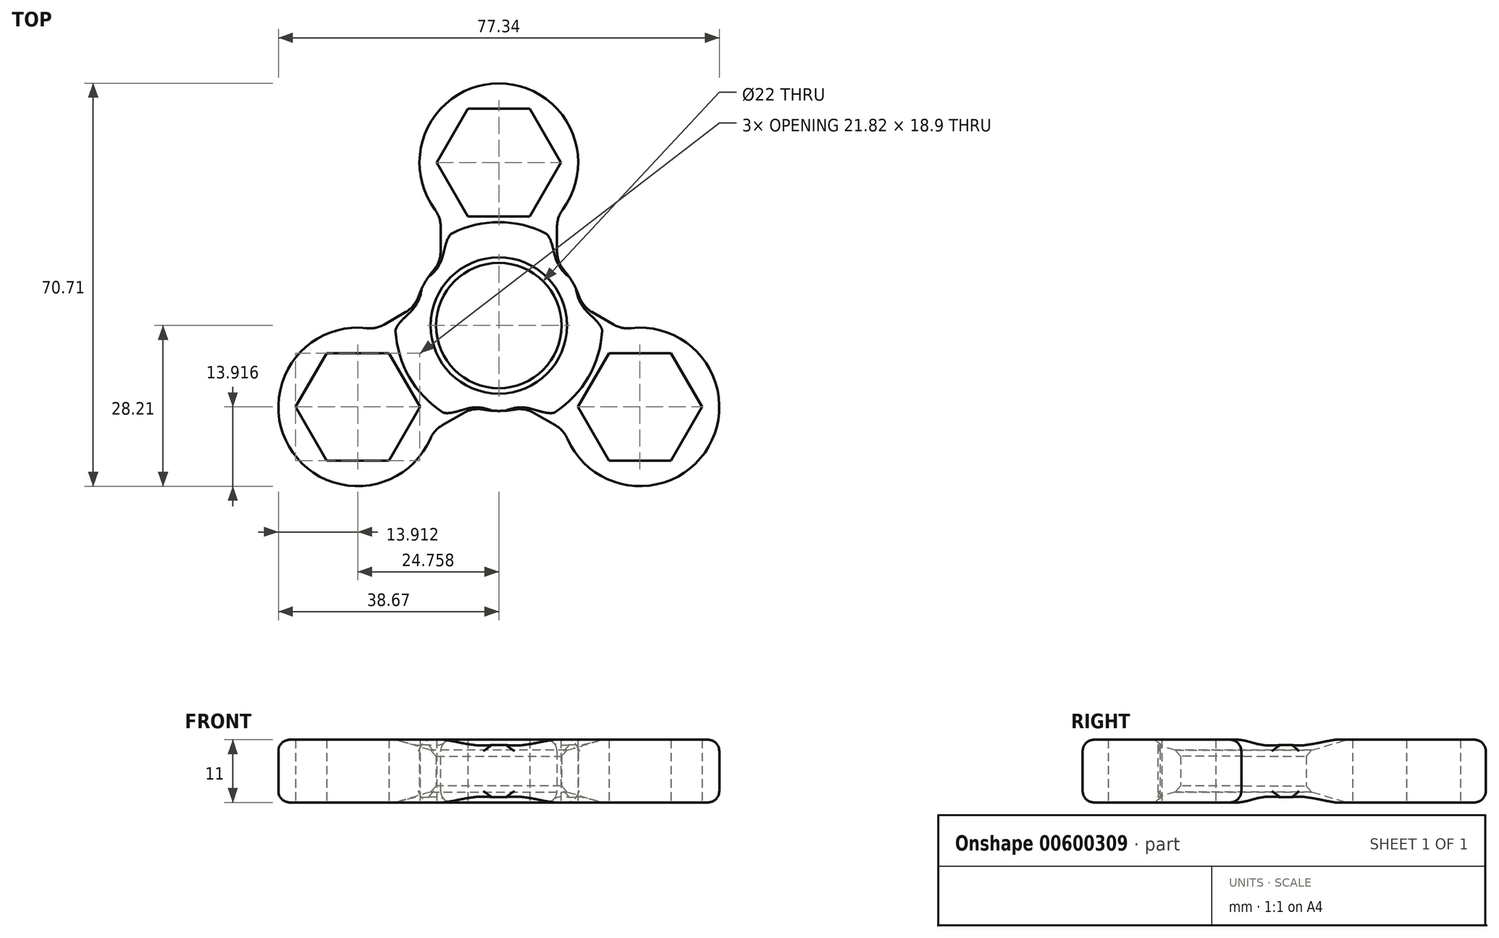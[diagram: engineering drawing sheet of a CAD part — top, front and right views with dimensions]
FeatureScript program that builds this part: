
annotation { "Feature Type Name" : "Feature", "Feature Type Description" : "" }
export const myFeature = defineFeature(function(context is Context, id is Id, definition is map)
    precondition{}
    {
        {
            var Q0;
            Q0=qCreatedBy(makeId("Top.planeOp"),FACE);
            var sketch = newSketch(context, id + "F0", { "sketchPlane" : qUnion([Q0])});
            skCircle(sketch, "E0", {"center": v(0, 0) * mm, "radius": 42.5 * mm, "construction": true});
            skLineSegment(sketch, "E1", {"start": v(0, 28.59) * mm, "end": v(0, 0) * mm, "construction": true});
            skLineSegment(sketch, "E2", {"start": v(0, 0) * mm, "end": v(-24.76, -14.3) * mm, "construction": true});
            skLineSegment(sketch, "E3", {"start": v(0, 0) * mm, "end": v(24.76, -14.3) * mm, "construction": true});
            skCircle(sketch, "E4.cCircle", {"center": v(0, 28.59) * mm, "radius": 9.45 * mm, "construction": true});
            skLineSegment(sketch, "E4.0", {"start": v(10.91, 28.59) * mm, "end": v(5.46, 19.14) * mm});
            skLineSegment(sketch, "E4.1", {"start": v(5.46, 19.14) * mm, "end": v(-5.46, 19.14) * mm});
            skLineSegment(sketch, "E4.2", {"start": v(-5.46, 19.14) * mm, "end": v(-10.91, 28.59) * mm});
            skLineSegment(sketch, "E4.3", {"start": v(-10.91, 28.59) * mm, "end": v(-5.46, 38.04) * mm});
            skLineSegment(sketch, "E4.4", {"start": v(-5.46, 38.04) * mm, "end": v(5.46, 38.04) * mm});
            skLineSegment(sketch, "E4.5", {"start": v(5.46, 38.04) * mm, "end": v(10.91, 28.59) * mm});
            skPoint(sketch, "E4.0.midPoint", {"position": v(8.18, 23.86) * mm});
            skArc(sketch, "E5.cCircle", {"start": v(10.2, 19.14) * mm, "mid": v(0, 42.5) * mm, "end": v(-10.2, 19.14) * mm});
            skLineSegment(sketch, "E6", {"start": v(-10.2, 19.14) * mm, "end": v(-10.2, 10.99) * mm});
            skLineSegment(sketch, "E7", {"start": v(10.2, 19.14) * mm, "end": v(10.2, 10.99) * mm});
            skCircle(sketch, "E8", {"center": v(0, 0) * mm, "radius": 11 * mm});
            skCircle(sketch, "E9.cCircle", {"center": v(24.76, -14.3) * mm, "radius": 9.45 * mm, "construction": true});
            skLineSegment(sketch, "E9.0", {"start": v(35.67, -14.3) * mm, "end": v(30.21, -23.74) * mm});
            skLineSegment(sketch, "E9.1", {"start": v(30.21, -23.74) * mm, "end": v(19.3, -23.74) * mm});
            skLineSegment(sketch, "E9.2", {"start": v(19.3, -23.74) * mm, "end": v(13.85, -14.3) * mm});
            skLineSegment(sketch, "E9.3", {"start": v(13.85, -14.3) * mm, "end": v(19.3, -4.84) * mm});
            skLineSegment(sketch, "E9.4", {"start": v(19.3, -4.84) * mm, "end": v(30.21, -4.84) * mm});
            skLineSegment(sketch, "E9.5", {"start": v(30.21, -4.84) * mm, "end": v(35.67, -14.3) * mm});
            skPoint(sketch, "E9.0.midPoint", {"position": v(32.94, -19.02) * mm});
            skArc(sketch, "E10.cCircle", {"start": v(11.47, -18.41) * mm, "mid": v(36.8, -21.25) * mm, "end": v(21.68, -0.73) * mm});
            skCircle(sketch, "E11.cCircle", {"center": v(-24.76, -14.3) * mm, "radius": 9.45 * mm, "construction": true});
            skLineSegment(sketch, "E11.0", {"start": v(-13.85, -14.3) * mm, "end": v(-19.3, -23.74) * mm});
            skLineSegment(sketch, "E11.1", {"start": v(-19.3, -23.74) * mm, "end": v(-30.21, -23.74) * mm});
            skLineSegment(sketch, "E11.2", {"start": v(-30.21, -23.74) * mm, "end": v(-35.67, -14.3) * mm});
            skLineSegment(sketch, "E11.3", {"start": v(-35.67, -14.3) * mm, "end": v(-30.21, -4.84) * mm});
            skLineSegment(sketch, "E11.4", {"start": v(-30.21, -4.84) * mm, "end": v(-19.3, -4.84) * mm});
            skLineSegment(sketch, "E11.5", {"start": v(-19.3, -4.84) * mm, "end": v(-13.85, -14.3) * mm});
            skPoint(sketch, "E11.0.midPoint", {"position": v(-16.57, -19.02) * mm});
            skArc(sketch, "E12.cCircle", {"start": v(-21.68, -0.73) * mm, "mid": v(-36.8, -21.25) * mm, "end": v(-11.47, -18.41) * mm});
            skLineSegment(sketch, "E13", {"start": v(-21.68, -0.73) * mm, "end": v(-14.62, 3.35) * mm});
            skLineSegment(sketch, "E14", {"start": v(-11.47, -18.41) * mm, "end": v(-4.41, -14.34) * mm});
            skLineSegment(sketch, "E15", {"start": v(11.47, -18.41) * mm, "end": v(4.41, -14.34) * mm});
            skLineSegment(sketch, "E16", {"start": v(21.68, -0.73) * mm, "end": v(14.62, 3.35) * mm});
            skArc(sketch, "E17", {"start": v(-10.2, 10.99) * mm, "mid": v(-13, 7.5) * mm, "end": v(-14.62, 3.35) * mm});
            skArc(sketch, "E18.trimOffspring", {"start": v(-4.41, -14.34) * mm, "mid": v(0, -15) * mm, "end": v(4.41, -14.34) * mm});
            skArc(sketch, "E19.trimOffspring", {"start": v(14.62, 3.35) * mm, "mid": v(13, 7.5) * mm, "end": v(10.2, 10.99) * mm});
            skSolve(sketch);
        }
        {
            var Q0;
            Q0=qSketchRegion(id+"F0",true);
            extrude(context, id + "F1", {"entities" : qUnion([Q0]), "endBound" : BoundingType.SYMMETRIC, "depth" : 11 * mm, "offsetDistance" : 25 * mm});
        }
        {
            var Q0;
            Q0=qCreatedBy(makeId("Right.planeOp"),FACE);
            var sketch = newSketch(context, id + "F2", { "sketchPlane" : qUnion([Q0])});
            skLineSegment(sketch, "E20", {"start": v(0, 0) * mm, "end": v(0, 13.53) * mm, "construction": true});
            skLineSegment(sketch, "E21.0", {"start": v(-11, 5.5) * mm, "end": v(11, 5.5) * mm, "construction": true});
            skLineSegment(sketch, "E22.0", {"start": v(19.14, 5.5) * mm, "end": v(19.14, -5.5) * mm, "construction": true});
            skLineSegment(sketch, "E23", {"start": v(18.14, 5.5) * mm, "end": v(11, 3.37) * mm});
            skLineSegment(sketch, "E24", {"start": v(11, 3.37) * mm, "end": v(11, 5.5) * mm});
            skLineSegment(sketch, "E25", {"start": v(11, 5.5) * mm, "end": v(18.14, 5.5) * mm});
            skLineSegment(sketch, "E26", {"start": v(18.14, -5.5) * mm, "end": v(11, -5.5) * mm});
            skLineSegment(sketch, "E27", {"start": v(11, -5.5) * mm, "end": v(11, -3.37) * mm});
            skLineSegment(sketch, "E28", {"start": v(11, -3.38) * mm, "end": v(18.14, -5.5) * mm});
            skSolve(sketch);
        }
        {
            var Q0;
            Q0=qSketchRegion(id+"F2",true);
            var Q1;
            Q1=sQuery(id+"F2.wireOp",EDGE,"E20");
            revolve(context, id + "F3", {"operationType" : NewBodyOperationType.REMOVE, "surfaceOperationType" : NewSurfaceOperationType.NEW, "entities" : qUnion([Q0]), "axis" : qUnion([Q1]), "revolveType" : RevolveType.FULL, "oppositeDirection" : true});
        }
        {
            var Q0;
            Q0=makeQuery(id+"F1.opExtrude","SWEPT_EDGE",EDGE,{"disambiguationData":[OSD([sQuery(id+"F0.wireOp",EDGE,"O4FCEVp2-a76e-EbQX-IVHh-MGuyo65jWMq8"),sQuery(id+"F0.wireOp",EDGE,"E6")])]});
            var Q1;
            Q1=makeQuery(id+"F1.opExtrude","SWEPT_EDGE",EDGE,{"disambiguationData":[OSD([sQuery(id+"F0.wireOp",EDGE,"O4FCEVp2-a76e-EbQX-IVHh-MGuyo65jWMq8"),sQuery(id+"F0.wireOp",EDGE,"E13")])]});
            var Q2;
            Q2=makeQuery(id+"F1.opExtrude","SWEPT_EDGE",EDGE,{"disambiguationData":[OSD([sQuery(id+"F0.wireOp",EDGE,"O4FCEVp2-a76e-EbQX-IVHh-MGuyo65jWMq8"),sQuery(id+"F0.wireOp",EDGE,"E15")])]});
            var Q3;
            Q3=makeQuery(id+"F1.opExtrude","SWEPT_EDGE",EDGE,{"disambiguationData":[OSD([sQuery(id+"F0.wireOp",EDGE,"O4FCEVp2-a76e-EbQX-IVHh-MGuyo65jWMq8"),sQuery(id+"F0.wireOp",EDGE,"E14")])]});
            var Q4;
            Q4=makeQuery(id+"F1.opExtrude","SWEPT_EDGE",EDGE,{"disambiguationData":[OSD([sQuery(id+"F0.wireOp",EDGE,"O4FCEVp2-a76e-EbQX-IVHh-MGuyo65jWMq8"),sQuery(id+"F0.wireOp",EDGE,"E16")])]});
            var Q5;
            Q5=makeQuery(id+"F1.opExtrude","SWEPT_EDGE",EDGE,{"disambiguationData":[OSD([sQuery(id+"F0.wireOp",EDGE,"O4FCEVp2-a76e-EbQX-IVHh-MGuyo65jWMq8"),sQuery(id+"F0.wireOp",EDGE,"E7")])]});
            var Q6;
            Q6=makeQuery(id+"F1.opExtrude","SWEPT_EDGE",EDGE,{"disambiguationData":[OSD([sQuery(id+"F0.wireOp",EDGE,"E10.4"),sQuery(id+"F0.wireOp",EDGE,"E10.5")])]});
            var Q7;
            Q7=makeQuery(id+"F1.opExtrude","SWEPT_EDGE",EDGE,{"disambiguationData":[OSD([sQuery(id+"F0.wireOp",EDGE,"E10.0"),sQuery(id+"F0.wireOp",EDGE,"E10.5")])]});
            var Q8;
            Q8=makeQuery(id+"F1.opExtrude","SWEPT_EDGE",EDGE,{"disambiguationData":[OSD([sQuery(id+"F0.wireOp",EDGE,"E10.0"),sQuery(id+"F0.wireOp",EDGE,"E10.1")])]});
            var Q9;
            Q9=makeQuery(id+"F1.opExtrude","SWEPT_EDGE",EDGE,{"disambiguationData":[OSD([sQuery(id+"F0.wireOp",EDGE,"E10.1"),sQuery(id+"F0.wireOp",EDGE,"E10.2")])]});
            var Q10;
            Q10=makeQuery(id+"F1.opExtrude","SWEPT_EDGE",EDGE,{"disambiguationData":[OSD([sQuery(id+"F0.wireOp",EDGE,"E12.0"),sQuery(id+"F0.wireOp",EDGE,"E12.1")])]});
            var Q11;
            Q11=makeQuery(id+"F1.opExtrude","SWEPT_EDGE",EDGE,{"disambiguationData":[OSD([sQuery(id+"F0.wireOp",EDGE,"E12.1"),sQuery(id+"F0.wireOp",EDGE,"E12.2")])]});
            var Q12;
            Q12=makeQuery(id+"F1.opExtrude","SWEPT_EDGE",EDGE,{"disambiguationData":[OSD([sQuery(id+"F0.wireOp",EDGE,"E12.2"),sQuery(id+"F0.wireOp",EDGE,"E12.3")])]});
            var Q13;
            Q13=makeQuery(id+"F1.opExtrude","SWEPT_EDGE",EDGE,{"disambiguationData":[OSD([sQuery(id+"F0.wireOp",EDGE,"E12.3"),sQuery(id+"F0.wireOp",EDGE,"E12.4")])]});
            var Q14;
            Q14=makeQuery(id+"F1.opExtrude","SWEPT_EDGE",EDGE,{"disambiguationData":[OSD([sQuery(id+"F0.wireOp",EDGE,"E5.2"),sQuery(id+"F0.wireOp",EDGE,"E5.3")])]});
            var Q15;
            Q15=makeQuery(id+"F1.opExtrude","SWEPT_EDGE",EDGE,{"disambiguationData":[OSD([sQuery(id+"F0.wireOp",EDGE,"E5.3"),sQuery(id+"F0.wireOp",EDGE,"E5.4")])]});
            var Q16;
            Q16=makeQuery(id+"F1.opExtrude","SWEPT_EDGE",EDGE,{"disambiguationData":[OSD([sQuery(id+"F0.wireOp",EDGE,"E5.4"),sQuery(id+"F0.wireOp",EDGE,"E5.5")])]});
            var Q17;
            Q17=makeQuery(id+"F1.opExtrude","SWEPT_EDGE",EDGE,{"disambiguationData":[OSD([sQuery(id+"F0.wireOp",EDGE,"E5.0"),sQuery(id+"F0.wireOp",EDGE,"E5.5")])]});
            fillet(context, id + "F4", {"entities" : qUnion([Q0, Q1, Q2, Q3, Q4, Q5, Q6, Q7, Q8, Q9, Q10, Q11, Q12, Q13, Q14, Q15, Q16, Q17]), "radius" : 5 * mm, "tangentPropagation" : true, "allowEdgeOverflow" : false});
        }
        {
            var Q0;
            Q0=makeQuery(id+"F1.opExtrude","CAP_EDGE",EDGE,{"disambiguationData":[OSD([sQuery(id+"F0.wireOp",EDGE,"E12.1")])],"isStart":false});
            var Q1;
            Q1=makeQuery(id+"F1.opExtrude","CAP_EDGE",EDGE,{"disambiguationData":[OSD([sQuery(id+"F0.wireOp",EDGE,"E12.1")])],"isStart":true});
            var Q2;
            Q2=makeQuery(id+"F3.boolean.opBoolean","INTERSECT",EDGE,{"derivedFrom":[makeQuery(id+"F1.opExtrude","SWEPT_FACE",FACE,{"disambiguationData":[OSD([sQuery(id+"F0.wireOp",EDGE,"E17")])]}),makeQuery(id+"F3.opRevolve","SWEPT_FACE",FACE,{"disambiguationData":[OSD([sQuery(id+"F2.wireOp",EDGE,"Kg2DwLSg-sN3A-W2FY-VowB-wog2JDw5YzpP")])]})]});
            var Q3;
            Q3=makeQuery(id+"F1.opExtrude","CAP_EDGE",EDGE,{"disambiguationData":[OSD([sQuery(id+"F0.wireOp",EDGE,"E5.3")])],"isStart":false});
            var Q4;
            Q4=makeQuery(id+"F3.boolean.opBoolean","INTERSECT",EDGE,{"derivedFrom":[makeQuery(id+"F1.opExtrude","SWEPT_FACE",FACE,{"disambiguationData":[OSD([sQuery(id+"F0.wireOp",EDGE,"E19.trimOffspring")])]}),makeQuery(id+"F3.opRevolve","SWEPT_FACE",FACE,{"disambiguationData":[OSD([sQuery(id+"F2.wireOp",EDGE,"Kg2DwLSg-sN3A-W2FY-VowB-wog2JDw5YzpP")])]})]});
            var Q5;
            Q5=makeQuery(id+"F1.opExtrude","CAP_EDGE",EDGE,{"disambiguationData":[OSD([sQuery(id+"F0.wireOp",EDGE,"E10.0")])],"isStart":false});
            var Q6;
            Q6=makeQuery(id+"F3.boolean.opBoolean","INTERSECT",EDGE,{"derivedFrom":[makeQuery(id+"F1.opExtrude","SWEPT_FACE",FACE,{"disambiguationData":[OSD([sQuery(id+"F0.wireOp",EDGE,"E18.trimOffspring")])]}),makeQuery(id+"F3.opRevolve","SWEPT_FACE",FACE,{"disambiguationData":[OSD([sQuery(id+"F2.wireOp",EDGE,"Kg2DwLSg-sN3A-W2FY-VowB-wog2JDw5YzpP")])]})]});
            var Q7;
            Q7=makeQuery(id+"F3.boolean.opBoolean","INTERSECT",EDGE,{"derivedFrom":[makeQuery(id+"F1.opExtrude","SWEPT_FACE",FACE,{"disambiguationData":[OSD([sQuery(id+"F0.wireOp",EDGE,"E18.trimOffspring")])]}),makeQuery(id+"F3.opRevolve","SWEPT_FACE",FACE,{"disambiguationData":[OSD([sQuery(id+"F2.wireOp",EDGE,"PyWXTRVD-vvde-1Qnd-1vty-Y3K4BUq7t7Ob")])]})]});
            var Q8;
            Q8=makeQuery(id+"F1.opExtrude","CAP_EDGE",EDGE,{"disambiguationData":[OSD([sQuery(id+"F0.wireOp",EDGE,"E10.0")])],"isStart":true});
            var Q9;
            Q9=makeQuery(id+"F1.opExtrude","CAP_EDGE",EDGE,{"disambiguationData":[OSD([sQuery(id+"F0.wireOp",EDGE,"E5.4")])],"isStart":true});
            var Q10;
            Q10=makeQuery(id+"F3.boolean.opBoolean","INTERSECT",EDGE,{"derivedFrom":[makeQuery(id+"F1.opExtrude","SWEPT_FACE",FACE,{"disambiguationData":[OSD([sQuery(id+"F0.wireOp",EDGE,"E19.trimOffspring")])]}),makeQuery(id+"F3.opRevolve","SWEPT_FACE",FACE,{"disambiguationData":[OSD([sQuery(id+"F2.wireOp",EDGE,"PyWXTRVD-vvde-1Qnd-1vty-Y3K4BUq7t7Ob")])]})]});
            var Q11;
            Q11=makeQuery(id+"F3.boolean.opBoolean","INTERSECT",EDGE,{"derivedFrom":[makeQuery(id+"F1.opExtrude","SWEPT_FACE",FACE,{"disambiguationData":[OSD([sQuery(id+"F0.wireOp",EDGE,"E17")])]}),makeQuery(id+"F3.opRevolve","SWEPT_FACE",FACE,{"disambiguationData":[OSD([sQuery(id+"F2.wireOp",EDGE,"PyWXTRVD-vvde-1Qnd-1vty-Y3K4BUq7t7Ob")])]})]});
            var Q12;
            Q12=makeQuery(id+"F1.opExtrude","CAP_EDGE",EDGE,{"disambiguationData":[OSD([sQuery(id+"F0.wireOp",EDGE,"E12.cCircle")])],"isStart":false});
            var Q13;
            Q13=makeQuery(id+"F1.opExtrude","CAP_EDGE",EDGE,{"disambiguationData":[OSD([sQuery(id+"F0.wireOp",EDGE,"E10.cCircle")])],"isStart":false});
            var Q14;
            Q14=makeQuery(id+"F1.opExtrude","CAP_EDGE",EDGE,{"disambiguationData":[OSD([sQuery(id+"F0.wireOp",EDGE,"E5.cCircle")])],"isStart":false});
            var Q15;
            Q15=makeQuery(id+"F1.opExtrude","CAP_EDGE",EDGE,{"disambiguationData":[OSD([sQuery(id+"F0.wireOp",EDGE,"E10.cCircle")])],"isStart":true});
            var Q16;
            Q16=makeQuery(id+"F1.opExtrude","CAP_EDGE",EDGE,{"disambiguationData":[OSD([sQuery(id+"F0.wireOp",EDGE,"E12.cCircle")])],"isStart":true});
            var Q17;
            Q17=makeQuery(id+"F1.opExtrude","CAP_EDGE",EDGE,{"disambiguationData":[OSD([sQuery(id+"F0.wireOp",EDGE,"E5.cCircle")])],"isStart":true});
            fillet(context, id + "F5", {"entities" : qUnion([Q0, Q1, Q2, Q3, Q4, Q5, Q6, Q7, Q8, Q9, Q10, Q11, Q12, Q13, Q14, Q15, Q16, Q17]), "radius" : 2 * mm, "tangentPropagation" : true, "allowEdgeOverflow" : false});
        }
        {
            var Q0;
            Q0=makeQuery(id+"F1.opExtrude","SWEPT_FACE",FACE,{"disambiguationData":[OSD([sQuery(id+"F0.wireOp",EDGE,"E8")])]});
            chamfer(context, id + "F6", {"entities" : qUnion([Q0]), "chamferType" : ChamferType.TWO_OFFSETS, "width1" : .75 * mm, "oppositeDirection" : false, "width2" : 1 * mm, "tangentPropagation" : true});
        }
    });
